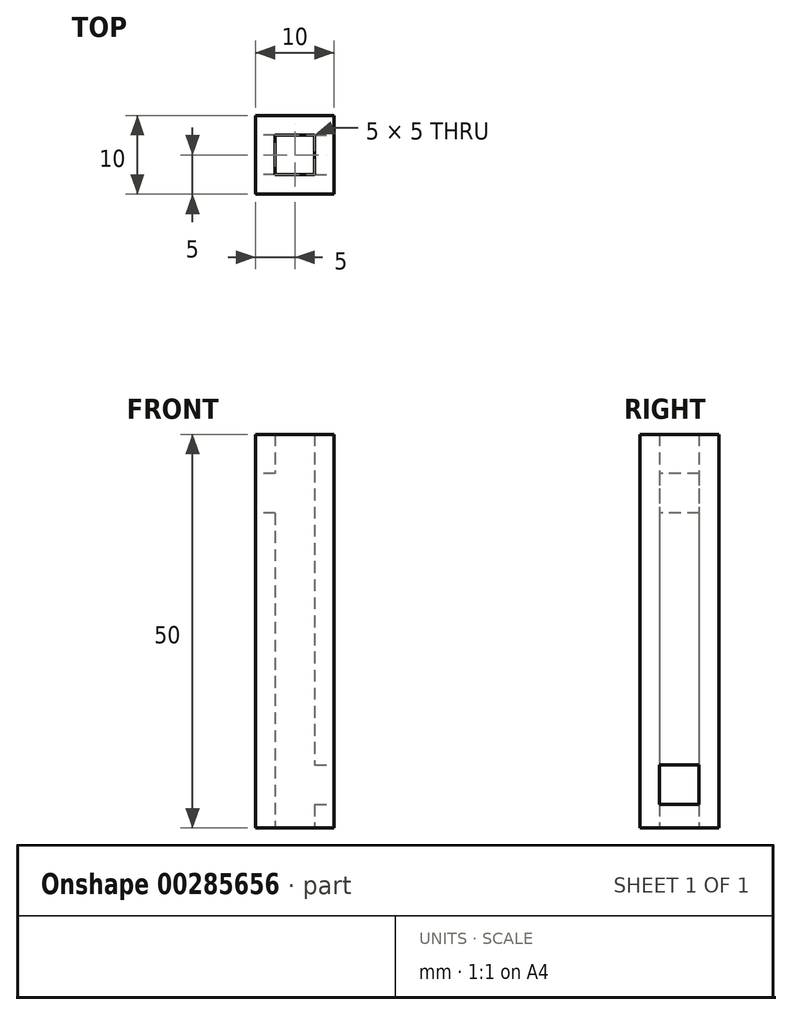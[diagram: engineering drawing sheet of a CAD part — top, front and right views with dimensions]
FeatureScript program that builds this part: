
annotation { "Feature Type Name" : "Feature", "Feature Type Description" : "" }
export const myFeature = defineFeature(function(context is Context, id is Id, definition is map)
    precondition{}
    {
        {
            var Q0;
            Q0=qCreatedBy(makeId("Top.planeOp"),FACE);
            var sketch = newSketch(context, id + "F0", { "sketchPlane" : qUnion([Q0])});
            skLineSegment(sketch, "E0.bottom", {"start": v(5, -5) * mm, "end": v(-5, -5) * mm});
            skLineSegment(sketch, "E0.top", {"start": v(5, 5) * mm, "end": v(-5, 5) * mm});
            skLineSegment(sketch, "E0.left", {"start": v(5, -5) * mm, "end": v(5, 5) * mm});
            skLineSegment(sketch, "E0.right", {"start": v(-5, -5) * mm, "end": v(-5, 5) * mm});
            skPoint(sketch, "E0.middle", {"position": v(0, 0) * mm});
            skLineSegment(sketch, "E1.bottom", {"start": v(2.5, -2.5) * mm, "end": v(-2.5, -2.5) * mm});
            skLineSegment(sketch, "E1.top", {"start": v(2.5, 2.5) * mm, "end": v(-2.5, 2.5) * mm});
            skLineSegment(sketch, "E1.left", {"start": v(2.5, -2.5) * mm, "end": v(2.5, 2.5) * mm});
            skLineSegment(sketch, "E1.right", {"start": v(-2.5, -2.5) * mm, "end": v(-2.5, 2.5) * mm});
            skSolve(sketch);
        }
        {
            var Q0;
            Q0 = qSketchRegion(id + "F0", true);
            extrude(context, id + "F1", {"entities" : qUnion([Q0]), "depth" : 50 * mm, "offsetDistance" : 25 * mm});
        }
        {
            var Q0;
            Q0=makeQuery(id+"F1.opExtrude","SWEPT_FACE",FACE,{"disambiguationData":[OSD([sQuery(id+"F0.wireOp",EDGE,"E0.left")])]});
            var sketch = newSketch(context, id + "F2", { "sketchPlane" : qUnion([Q0])});
            skLineSegment(sketch, "E2.bottom", {"start": v(2.5, 8) * mm, "end": v(-2.5, 8) * mm});
            skLineSegment(sketch, "E2.top", {"start": v(2.5, 3) * mm, "end": v(-2.5, 3) * mm});
            skLineSegment(sketch, "E2.left", {"start": v(2.5, 8) * mm, "end": v(2.5, 3) * mm});
            skLineSegment(sketch, "E2.right", {"start": v(-2.5, 8) * mm, "end": v(-2.5, 3) * mm});
            skPoint(sketch, "E2.middle", {"position": v(0, 5.5) * mm});
            skSolve(sketch);
        }
        {
            var Q0;
            Q0=makeQuery(id+"F2.imprint","IMPRINT",FACE,{"disambiguationData":[TD([[makeQuery(id+"F2.imprint","IMPRINT",EDGE,{"derivedFrom":sQuery(id+"F2.wireOp",EDGE,"E2.bottom")}),1.0]])]});
            var Q1;
            Q1=makeQuery(id+"F1.opExtrude","SWEPT_FACE",FACE,{"disambiguationData":[OSD([sQuery(id+"F0.wireOp",EDGE,"E0.right")])]});
            extrude(context, id + "F3", {"entities" : qUnion([Q0, Q1]), "operationType" : NewBodyOperationType.REMOVE, "oppositeDirection" : true, "depth" : 3 * mm, "offsetDistance" : 25 * mm});
        }
        {
            var Q0;
            Q0=makeQuery(id+"F1.opExtrude","SWEPT_FACE",FACE,{"disambiguationData":[OSD([sQuery(id+"F0.wireOp",EDGE,"E0.right")])]});
            var sketch = newSketch(context, id + "F4", { "sketchPlane" : qUnion([Q0])});
            skLineSegment(sketch, "E3.bottom", {"start": v(-2.5, 45) * mm, "end": v(2.5, 45) * mm});
            skLineSegment(sketch, "E3.top", {"start": v(-2.5, 40) * mm, "end": v(2.5, 40) * mm});
            skLineSegment(sketch, "E3.left", {"start": v(-2.5, 45) * mm, "end": v(-2.5, 40) * mm});
            skLineSegment(sketch, "E3.right", {"start": v(2.5, 45) * mm, "end": v(2.5, 40) * mm});
            skPoint(sketch, "E3.middle", {"position": v(0, 42.5) * mm});
            skSolve(sketch);
        }
        {
            var Q0;
            Q0=makeQuery(id+"F4.imprint","IMPRINT",FACE,{"disambiguationData":[TD([[makeQuery(id+"F4.imprint","IMPRINT",EDGE,{"derivedFrom":sQuery(id+"F4.wireOp",EDGE,"E3.bottom")}),-1.0]])]});
            extrude(context, id + "F5", {"entities" : qUnion([Q0]), "operationType" : NewBodyOperationType.REMOVE, "oppositeDirection" : true, "depth" : 4 * mm, "offsetDistance" : 25 * mm});
        }
    });
